# Revit family: JAD_Neon_A5567_BIM_DE
name_source: partatom
category: Plumbing Fixtures
revit_build: Autodesk Revit 2015 (Build: 20140606_1530(x64)
units: mm (PartAtom-declared; Revit-internal decimal feet)

## types (1)
- A5567AA - NEON BSN MXR R-MTD CHR SPT/120 PU/MET
    Accessories = www.idealspec.co.uk
    AreaUnits = millimeters
    Assembly Code = C1030200
    AssetType = Fixed
    BIMObjectName = JAD_Jado_WashbasinTaps_Neon_A5567
    BarCode = 4015413326056
    Brand = Ideal Standard
    Color = Chromium Plated
    ConnectionType = Plumbing
    Cost = 0 $
    Description = NEON BSN MXR R-MTD CHR SPT/120 PU/MET
    DurationUnit = year
    Features = NEON BSN MXR R-MTD CHR SPT/120 PU/MET
    Finish = Chromium Plated
    Help = www.idealstandard.de
    IfcExportAs = IfcValveType
    IfcExportType = BASIN MIXER
    InstallationInstructions = www.idealstandard.de
    LinearUnits = millimeters
    MainColor = Chromium Plated
    MaintenanceInformation = www.idealstandard.de
    Manufacturer = www.idealstandard.de
    ManufacturerURL = www.idealstandard.de
    Model = A5567AA
    ModelNumber = A5567AA
    ModelReference = NEON BSN MXR R-MTD CHR SPT/120 PU/MET
    Name = WashbasinTaps_Neon_A5567_JAD
    NettWeight = 2,65 KG
    NominalDepth = 625 mm
    NominalHeight = 93 mm
    NominalLength = 625 mm
    NominalWidth = 250 mm
    ProductInformation = www.idealstandard.de
    Shape = Sculptured
    Size = 93 x 625 x 250 mm
    Space = Internal
    SpareParts = www.idealstandard.de
    TestPressure = 10 bar
    URL = www.idealstandard.de
    Uniclass2015Code = Pr_40_20_87_98
    Uniclass2015Title = Washbasin taps
    Uniclass2015Version = Products v1.1

## geometry (parser evidence)
native form markers: Blend x4
no freeform markers — native parametric forms only
